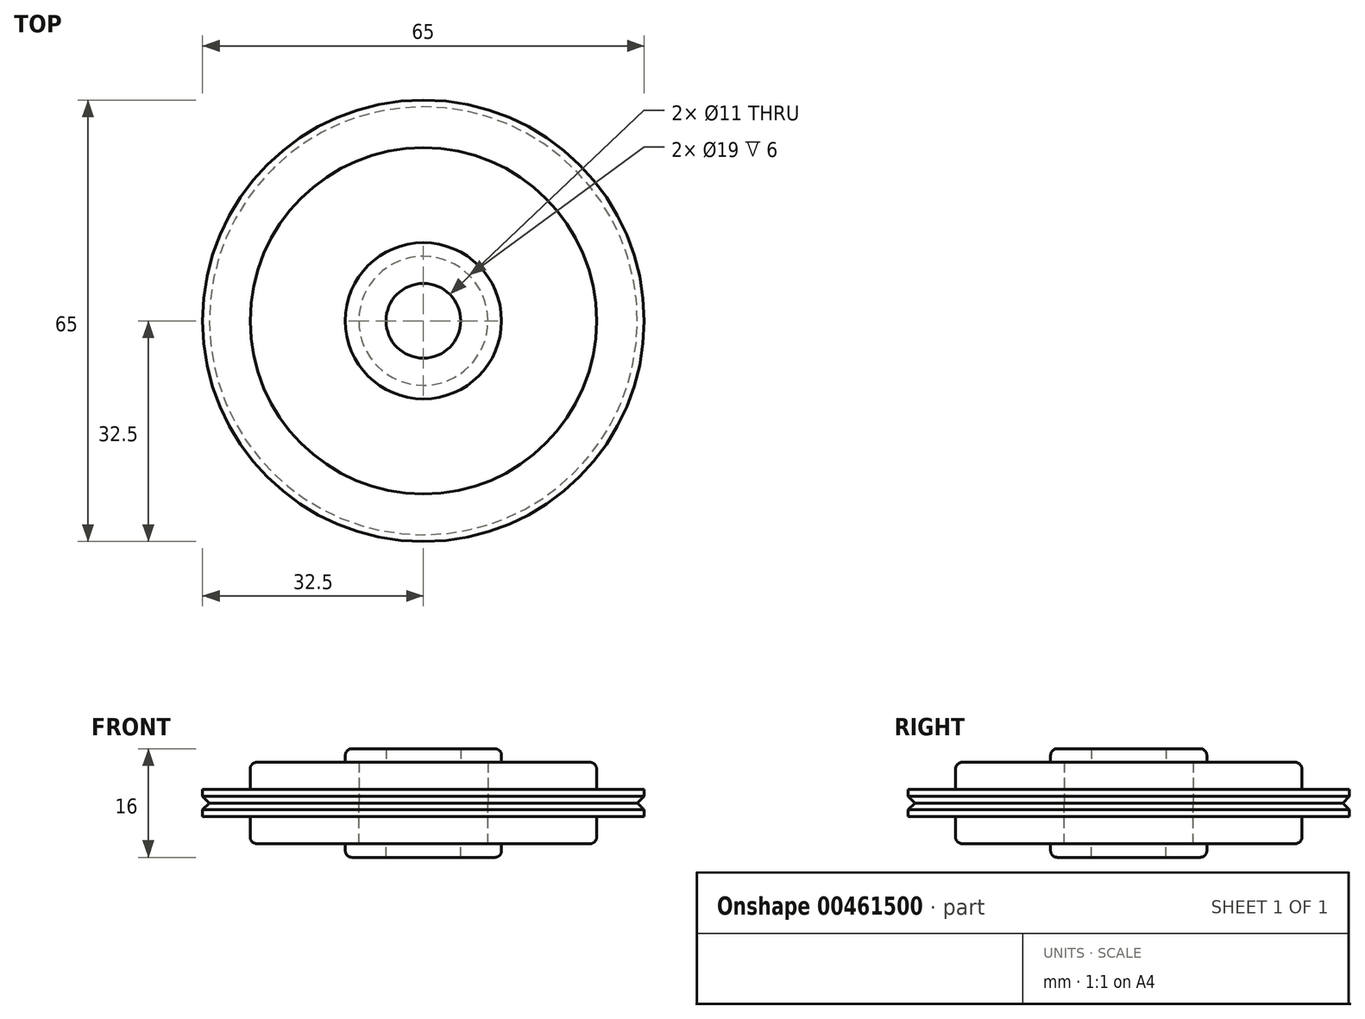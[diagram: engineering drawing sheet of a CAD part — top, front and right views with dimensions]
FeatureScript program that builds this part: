
annotation { "Feature Type Name" : "Feature", "Feature Type Description" : "" }
export const myFeature = defineFeature(function(context is Context, id is Id, definition is map)
    precondition{}
    {
        {
            var Q0;
            Q0=qCreatedBy(makeId("Top.planeOp"),FACE);
            var sketch = newSketch(context, id + "F0", { "sketchPlane" : qUnion([Q0])});
            skCircle(sketch, "E0", {"center": v(0, 0) * mm, "radius": 32.5 * mm});
            skCircle(sketch, "E1", {"center": v(0, 0) * mm, "radius": 25.5 * mm});
            skCircle(sketch, "E2", {"center": v(0, 0) * mm, "radius": 9.5 * mm});
            skCircle(sketch, "E3", {"center": v(0, 0) * mm, "radius": 11.5 * mm});
            skCircle(sketch, "E4", {"center": v(0, 0) * mm, "radius": 5.5 * mm});
            skSolve(sketch);
        }
        {
            var Q0;
            Q0=makeQuery(id+"F0.imprint","IMPRINT",FACE,{"disambiguationData":[TD([[makeQuery(id+"F0.imprint","IMPRINT",EDGE,{"derivedFrom":sQuery(id+"F0.wireOp",EDGE,"E0")}),1.0]])]});
            extrude(context, id + "F1", {"entities" : qUnion([Q0]), "depth" : 2 * mm});
        }
        {
            var Q0;
            Q0=makeQuery(id+"F0.imprint","IMPRINT",FACE,{"disambiguationData":[TD([[makeQuery(id+"F0.imprint","IMPRINT",EDGE,{"derivedFrom":sQuery(id+"F0.wireOp",EDGE,"E1")}),1.0]])]});
            extrude(context, id + "F2", {"entities" : qUnion([Q0]), "operationType" : NewBodyOperationType.ADD, "depth" : 6 * mm});
        }
        {
            var Q0;
            Q0=makeQuery(id+"F0.imprint","IMPRINT",FACE,{"disambiguationData":[TD([[makeQuery(id+"F0.imprint","IMPRINT",EDGE,{"derivedFrom":sQuery(id+"F0.wireOp",EDGE,"E2")}),-1.0]])]});
            extrude(context, id + "F3", {"entities" : qUnion([Q0]), "operationType" : NewBodyOperationType.ADD, "depth" : 8 * mm});
        }
        {
            var Q0;
            Q0=makeQuery(id+"F0.imprint","IMPRINT",FACE,{"disambiguationData":[TD([[makeQuery(id+"F0.imprint","IMPRINT",EDGE,{"derivedFrom":sQuery(id+"F0.wireOp",EDGE,"E2")}),1.0]])]});
            extrude(context, id + "F4", {"entities" : qUnion([Q0]), "operationType" : NewBodyOperationType.ADD, "depth" : 8 * mm});
        }
        {
            var Q0;
            Q0=makeQuery(id+"F0.imprint","IMPRINT",FACE,{"disambiguationData":[TD([[makeQuery(id+"F0.imprint","IMPRINT",EDGE,{"derivedFrom":sQuery(id+"F0.wireOp",EDGE,"E2")}),1.0]])]});
            extrude(context, id + "F5", {"entities" : qUnion([Q0]), "operationType" : NewBodyOperationType.REMOVE, "oppositeDirection" : true, "depth" : -6 * mm});
        }
        {
            var Q0;
            Q0=makeQuery(id+"F3.opExtrude","CAP_EDGE",EDGE,{"disambiguationData":[OSD([sQuery(id+"F0.wireOp",EDGE,"E3")])],"isStart":false});
            fillet(context, id + "F6", {"entities" : qUnion([Q0]), "radius" : 1 * mm, "tangentPropagation" : true, "allowEdgeOverflow" : false});
        }
        {
            var Q0;
            Q0=makeQuery(id+"F2.opExtrude","CAP_EDGE",EDGE,{"disambiguationData":[OSD([sQuery(id+"F0.wireOp",EDGE,"E1")])],"isStart":false});
            fillet(context, id + "F7", {"entities" : qUnion([Q0]), "radius" : 1 * mm, "tangentPropagation" : true, "allowEdgeOverflow" : false});
        }
        {
            var Q0;
            Q0=makeQuery(id+"F1.opExtrude","CAP_EDGE",EDGE,{"disambiguationData":[OSD([sQuery(id+"F0.wireOp",EDGE,"E0")])],"isStart":true});
            chamfer(context, id + "F8", {"entities" : qUnion([Q0]), "width" : 1 * mm, "tangentPropagation" : true});
        }
        {
            var Q0;
            Q0=makeQuery(id+"F1.opExtrude","SWEPT_BODY",BODY,{"disambiguationData":[OSD([sQuery(id+"F0.wireOp",EDGE,"E0"),sQuery(id+"F0.wireOp",EDGE,"E1")])]});
            var Q1;
            Q1=makeQuery(id+"F0.imprint","IMPRINT",FACE,{"disambiguationData":[TD([[makeQuery(id+"F0.imprint","IMPRINT",EDGE,{"derivedFrom":sQuery(id+"F0.wireOp",EDGE,"E1")}),1.0]])]});
            mirror(context, id + "F9", {"entities" : qUnion([Q0]), "mirrorPlane" : qUnion([Q1])});
        }
    });
